# Revit family: 3097182 Lighting Fixture_Sylvania_Insaver LED 150 LO-Low Profile_Ceiling Recessed
name_source: partatom
category: Lighting Fixtures
revit_build: Autodesk Revit 2017 (Build: 20190507_1515(x64)
units: mm (PartAtom-declared; Revit-internal decimal feet)

## family parameters
Cut with Voids When Loaded = No
Host = Face
Light Source = Yes
OmniClass Number = 23.80.70.11.17
OmniClass Title = Specialized Lighting by Location or Use
Part Type = Normal
Room Calculation Point = No
Round Connector Dimension = Use Diameter
Shared = No

## types (2) — shared parameters
Accessory Material = Aluminum_Sylvania_Insaver 150 LED_White
Apparent Load = 19 VA
Assembly Code = D5020200
Beam Angle = Wide
CRI ( Ra ) = 75
Color Filter = 16777215
Connector Width = 60 mm
Description = New updated midpower LED chips, High light output up to 2,200lm High efficacy - up to 73lm/W Low weight, facetted, scratch-resistant polycarbonate reflector 2 versions: low recess depth (<100mm) and low glare
Diffuser Material = Polycarbonate_Sylvania_Insaver 150 LED_Opal
Dimming Lamp Color Temperature Shift = <None>
Drive Current = 700mA
Electrical Protection = CLASS II
Emit Shape Visible in Rendering = No
Glow Wire Test = 650 °C
Height = 100 mm  [stored 0.328084 ft]
IP Rating = IP44
Lamp = Mid Power LEDs
Lamp Comments = Integrated LED
Life = 50 000
Manufacturer = Feilo Sylvania
Product Family = INSAVER LED 150 LO - LOW PROFILE
Product Page URL = http://www.sylvania-lighting.com
Recessed Depth = 100 mm  [stored 0.328084 ft]
Reflector Material = Polycarbonate_Sylvania_Insaver 150 LED_Silver
T Class Max = -1 °C
T Class Min = -1 °C
Tilt Angle = -90.00°
Transformator Material = Aluminum_Sylvania_Insaver 150 LED_Black
URL = http://www.sylvania-lighting.com
Voltage = 240 V
Voltage Comments = UNV (Universal Voltage; 220-240 Volt)
Weight = 1.20 kg
zero-valued in all types: Default Elevation

## per-type parameters (varying)
| type | Connector Length | Cutout Diameter | Diameter | Emit from Circle Diameter | Inner Diameter | Inner Radius | Model | Photometric Web File |
| Insaver 150 LED RS 19W WW EB WH | 103 mm  [stored 0.337927 ft] | 152 mm  [stored 0.498688 ft] | 167 mm  [stored 0.5479 ft] | 148 mm | 148 mm | 74 mm | 3097182 Insaver 150 LED RS 19W WW EB WH | 3097182_Insaver150LEDRS19WWWEBWH-98726.ies |
| Insaver 150 LED RS 19W NW EB WH | 101 mm | 150 mm | 165 mm | 146 mm  [stored 0.479003 ft] | 146 mm  [stored 0.479003 ft] | 73 mm  [stored 0.239501 ft] | 3097183 Insaver 150 LED RS 19W NW EB WH | 3097183_Insaver150LEDRS19WNWEBWH-98848.ies |

note: [stored X ft] marks values corroborated as IEEE doubles in the binary element streams (Revit-internal decimal feet)

## geometry (parser evidence)
native form markers: Blend x8, Sweep x1
no freeform markers — native parametric forms only
